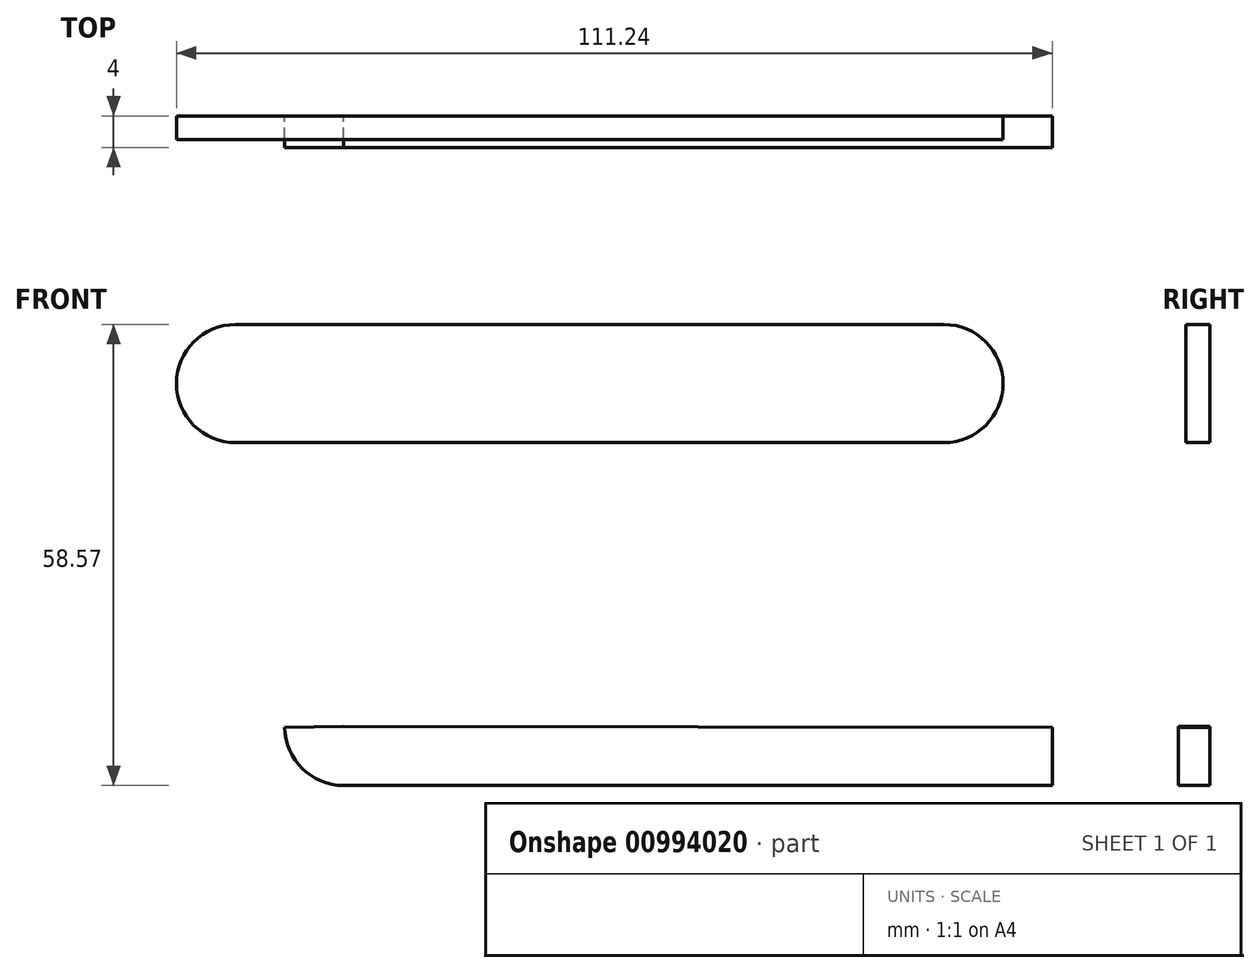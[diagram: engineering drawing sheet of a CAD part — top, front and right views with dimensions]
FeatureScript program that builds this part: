
annotation { "Feature Type Name" : "Feature", "Feature Type Description" : "" }
export const myFeature = defineFeature(function(context is Context, id is Id, definition is map)
    precondition{}
    {
        {
            var Q0;
            Q0=qCreatedBy(makeId("Front.planeOp"),FACE);
            var sketch = newSketch(context, id + "F0", { "sketchPlane" : qUnion([Q0])});
            skLineSegment(sketch, "E0.bottom", {"start": v(-42.64, -7.1) * mm, "end": v(47.36, -7.1) * mm});
            skLineSegment(sketch, "E0.top", {"start": v(-42.64, 7.9) * mm, "end": v(47.36, 7.9) * mm});
            skLineSegment(sketch, "E0.left", {"start": v(-42.64, -7.1) * mm, "end": v(-42.64, 7.9) * mm});
            skLineSegment(sketch, "E0.right", {"start": v(47.36, -7.1) * mm, "end": v(47.36, -1.1) * mm});
            skArc(sketch, "E1", {"start": v(47.36, -7.1) * mm, "mid": v(54.86, 0.4) * mm, "end": v(47.36, 7.9) * mm});
            skArc(sketch, "E2", {"start": v(-42.64, 7.9) * mm, "mid": v(-50.14, 0.4) * mm, "end": v(-42.64, -7.1) * mm});
            skCircle(sketch, "E3", {"center": v(47.36, 0.4) * mm, "radius": 1.5 * mm});
            skLineSegment(sketch, "E4", {"start": v(-31.95, 0.3) * mm, "end": v(-50.14, 0.3) * mm});
            skLineSegment(sketch, "E5", {"start": v(-31.95, 0.3) * mm, "end": v(45.87, 0.3) * mm});
            skLineSegment(sketch, "E6", {"start": v(-31.95, 0.3) * mm, "end": v(-31.95, -7.1) * mm, "construction": true});
            skLineSegment(sketch, "E7.bottom", {"start": v(-28.9, -50.67) * mm, "end": v(61.1, -50.67) * mm});
            skLineSegment(sketch, "E7.left", {"start": v(-28.9, -50.67) * mm, "end": v(-28.9, -43.17) * mm});
            skLineSegment(sketch, "E7.right", {"start": v(61.1, -50.67) * mm, "end": v(61.1, -43.27) * mm});
            skArc(sketch, "E8", {"start": v(-36.4, -43.27) * mm, "mid": v(-34.17, -48.5) * mm, "end": v(-28.9, -50.67) * mm});
            skLineSegment(sketch, "E9.trimOffspring", {"start": v(47.36, 1.9) * mm, "end": v(47.36, 7.9) * mm});
            skLineSegment(sketch, "E10.top", {"start": v(-67.27, 55.86) * mm, "end": v(22.73, 55.86) * mm});
            skLineSegment(sketch, "E11", {"start": v(-67.27, 55.86) * mm, "end": v(-67.27, 63.36) * mm});
            skArc(sketch, "E12", {"start": v(-67.27, 63.36) * mm, "mid": v(-72.57, 61.16) * mm, "end": v(-74.77, 55.86) * mm});
            skLineSegment(sketch, "E13", {"start": v(-67.27, 55.86) * mm, "end": v(-74.77, 55.86) * mm});
            skLineSegment(sketch, "E14", {"start": v(-67.27, 63.36) * mm, "end": v(22.73, 63.36) * mm});
            skLineSegment(sketch, "E15", {"start": v(22.73, 63.36) * mm, "end": v(22.73, 55.86) * mm});
            skLineSegment(sketch, "E16", {"start": v(-36.4, -43.27) * mm, "end": v(-28.9, -43.17) * mm});
            skLineSegment(sketch, "E17", {"start": v(-28.9, -43.17) * mm, "end": v(61.1, -43.27) * mm});
            skSolve(sketch);
        }
        {
            var Q0;
            Q0=makeQuery(id+"F0.imprint","IMPRINT",FACE,{"disambiguationData":[TD([[makeQuery(id+"F0.imprint","IMPRINT",EDGE,{"derivedFrom":sQuery(id+"F0.wireOp",EDGE,"E7.bottom")}),1.0]])]});
            var Q1;
            Q1=makeQuery(id+"F0.imprint","IMPRINT",FACE,{"disambiguationData":[TD([[makeQuery(id+"F0.imprint","IMPRINT",EDGE,{"derivedFrom":sQuery(id+"F0.wireOp",EDGE,"E7.left")}),1.0]])]});
            extrude(context, id + "F1", {"entities" : qUnion([Q0, Q1]), "depth" : 4 * mm, "offsetDistance" : 25 * mm});
        }
        {
            var Q0;
            {var subQ0=sQuery(id+"F0.wireOp",EDGE,"E2");var subQ3=sQuery(id+"F0.wireOp",EDGE,"E4");var subQ5=makeQuery(id+"F0.imprint","INTERSECT",VERTEX,{"derivedFrom":[subQ0,subQ3]});Q0=makeQuery(id+"F0.imprint","IMPRINT",FACE,{"disambiguationData":[TD([[makeQuery(id+"F0.imprint","IMPRINT",EDGE,{"disambiguationData":[TD([[subQ5,1.0]])],"derivedFrom":subQ3}),1.0]])]});}
            var Q1;
            {var subQ0=sQuery(id+"F0.wireOp",EDGE,"E2");var subQ3=sQuery(id+"F0.wireOp",EDGE,"E4");var subQ5=makeQuery(id+"F0.imprint","INTERSECT",VERTEX,{"derivedFrom":[subQ0,subQ3]});Q1=makeQuery(id+"F0.imprint","IMPRINT",FACE,{"disambiguationData":[TD([[makeQuery(id+"F0.imprint","IMPRINT",EDGE,{"disambiguationData":[TD([[subQ5,1.0]])],"derivedFrom":subQ3}),-1.0]])]});}
            var Q2;
            {var subQ0=sQuery(id+"F0.wireOp",EDGE,"E0.right");Q2=makeQuery(id+"F0.imprint","IMPRINT",FACE,{"disambiguationData":[TD([[makeQuery(id+"F0.imprint","IMPRINT",EDGE,{"derivedFrom":subQ0}),-1.0]])]});}
            var Q3;
            {var subQ4=sQuery(id+"F0.wireOp",EDGE,"E0.bottom");Q3=makeQuery(id+"F0.imprint","IMPRINT",FACE,{"disambiguationData":[TD([[makeQuery(id+"F0.imprint","IMPRINT",EDGE,{"derivedFrom":subQ4}),1.0]])]});}
            var Q4;
            {var subQ4=sQuery(id+"F0.wireOp",EDGE,"E0.top");Q4=makeQuery(id+"F0.imprint","IMPRINT",FACE,{"disambiguationData":[TD([[makeQuery(id+"F0.imprint","IMPRINT",EDGE,{"derivedFrom":subQ4}),-1.0]])]});}
            var Q5;
            {var subQ0=sQuery(id+"F0.wireOp",EDGE,"E3");var subQ1=makeQuery(id+"F0.imprint","INTERSECT",VERTEX,{"derivedFrom":[subQ0,sQuery(id+"F0.wireOp",EDGE,"E5")]});Q5=makeQuery(id+"F0.imprint","IMPRINT",FACE,{"disambiguationData":[TD([[makeQuery(id+"F0.imprint","IMPRINT",EDGE,{"disambiguationData":[TD([[subQ1,1.0]])],"derivedFrom":subQ0}),1.0]])]});}
            extrude(context, id + "F2", {"entities" : qUnion([Q0, Q1, Q2, Q3, Q4, Q5]), "depth" : 3 * mm, "offsetDistance" : 25 * mm});
        }
    });
